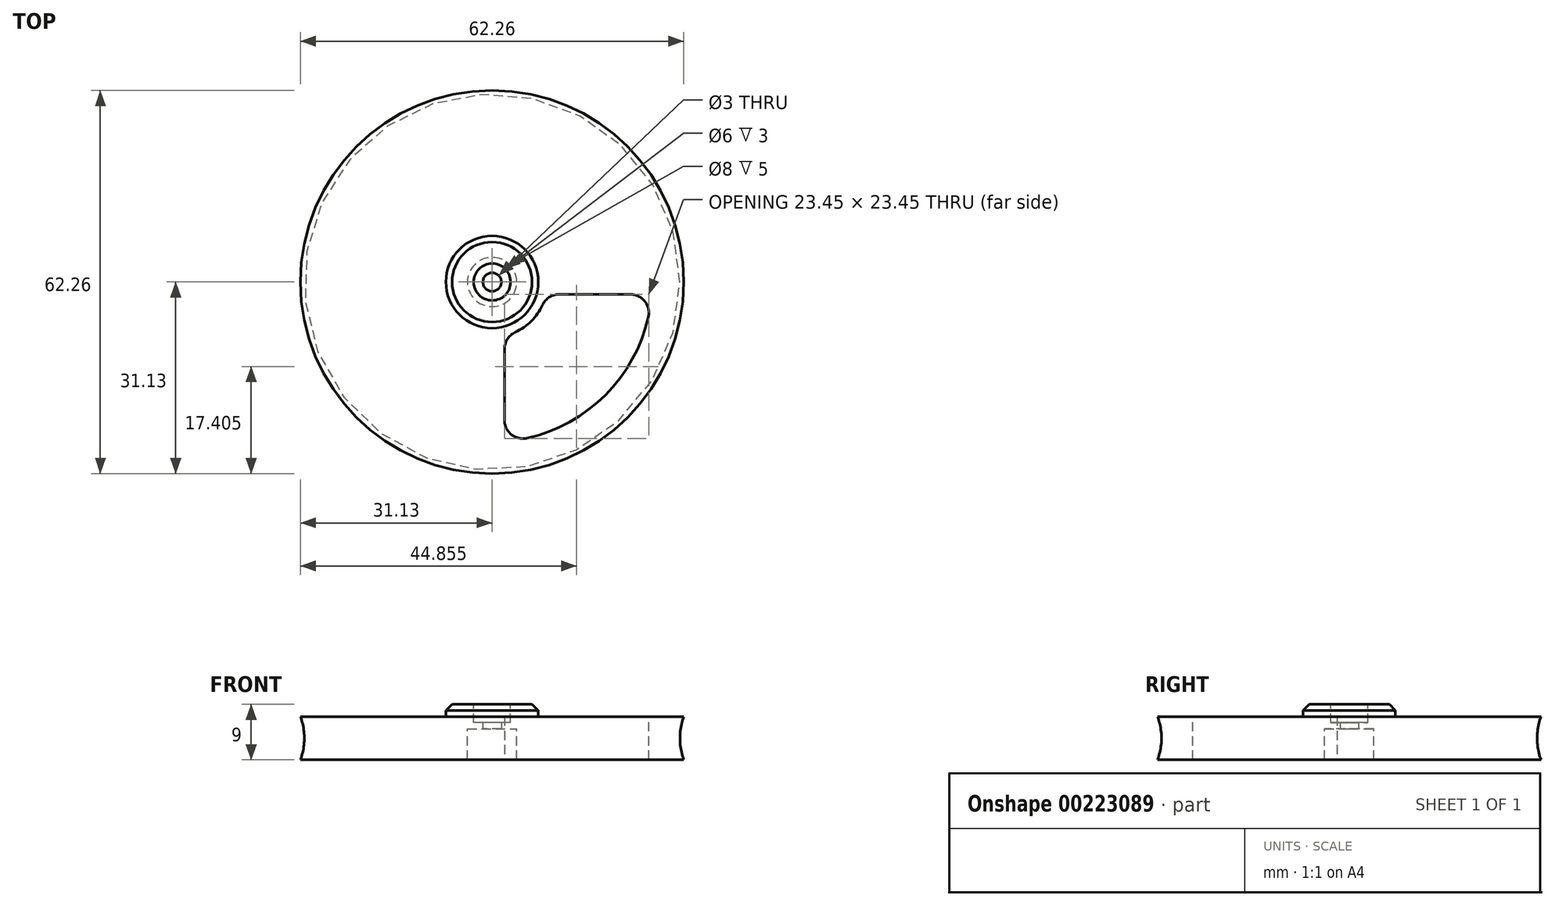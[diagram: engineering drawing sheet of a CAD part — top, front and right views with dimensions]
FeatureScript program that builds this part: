
annotation { "Feature Type Name" : "Feature", "Feature Type Description" : "" }
export const myFeature = defineFeature(function(context is Context, id is Id, definition is map)
    precondition{}
    {
        {
            var Q0;
            Q0=qCreatedBy(makeId("Top.planeOp"),FACE);
            var sketch = newSketch(context, id + "F0", { "sketchPlane" : qUnion([Q0])});
            skCircle(sketch, "E0", {"center": v(0, 0) * mm, "radius": 30 * mm});
            skCircle(sketch, "E1", {"center": v(0, 0) * mm, "radius": 1.5 * mm});
            skSolve(sketch);
        }
        {
            var Q0;
            Q0=makeQuery(id+"F0.imprint","IMPRINT",FACE,{"disambiguationData":[TD([[makeQuery(id+"F0.imprint","IMPRINT",EDGE,{"derivedFrom":sQuery(id+"F0.wireOp",EDGE,"E0")}),1.0]])]});
            extrude(context, id + "F1", {"entities" : qUnion([Q0]), "depth" : 2 * mm});
        }
        {
            var Q0;
            Q0=makeQuery(id+"F1.opExtrude","CAP_FACE",FACE,{"disambiguationData":[OSD([sQuery(id+"F0.wireOp",EDGE,"E0"),sQuery(id+"F0.wireOp",EDGE,"E1")])],"isStart":false});
            var sketch = newSketch(context, id + "F2", { "sketchPlane" : qUnion([Q0])});
            skCircle(sketch, "E2", {"center": v(0, 0) * mm, "radius": 7.5 * mm});
            skSolve(sketch);
        }
        {
            var Q0;
            Q0=makeQuery(id+"F2.imprint","IMPRINT",FACE,{"disambiguationData":[TD([[makeQuery(id+"F2.imprint","IMPRINT",EDGE,{"derivedFrom":sQuery(id+"F2.wireOp",EDGE,"E2")}),1.0]])]});
            extrude(context, id + "F3", {"entities" : qUnion([Q0]), "operationType" : NewBodyOperationType.ADD, "depth" : 2 * mm});
        }
        {
            var Q0;
            Q0=makeQuery(id+"F3.opExtrude","CAP_FACE",FACE,{"disambiguationData":[OSD([sQuery(id+"F0.wireOp",EDGE,"E1"),sQuery(id+"F2.wireOp",EDGE,"E2")])],"isStart":false});
            var sketch = newSketch(context, id + "F4", { "sketchPlane" : qUnion([Q0])});
            skCircle(sketch, "E3", {"center": v(0, 0) * mm, "radius": 3 * mm});
            skSolve(sketch);
        }
        {
            var Q0;
            Q0=makeQuery(id+"F4.imprint","IMPRINT",FACE,{"disambiguationData":[TD([[makeQuery(id+"F4.imprint","IMPRINT",EDGE,{"derivedFrom":sQuery(id+"F4.wireOp",EDGE,"E3")}),1.0]])]});
            extrude(context, id + "F5", {"entities" : qUnion([Q0]), "operationType" : NewBodyOperationType.REMOVE, "oppositeDirection" : true, "depth" : 3 * mm});
        }
        {
            var Q0;
            Q0=makeQuery(id+"F3.opExtrude","CAP_EDGE",EDGE,{"disambiguationData":[OSD([sQuery(id+"F2.wireOp",EDGE,"E2")])],"isStart":false});
            chamfer(context, id + "F6", {"entities" : qUnion([Q0]), "width" : 1 * mm, "tangentPropagation" : true});
        }
        {
            var Q0;
            Q0=makeQuery(id+"F1.opExtrude","CAP_FACE",FACE,{"disambiguationData":[OSD([sQuery(id+"F0.wireOp",EDGE,"E0"),sQuery(id+"F0.wireOp",EDGE,"E1")])],"isStart":true});
            var sketch = newSketch(context, id + "F7", { "sketchPlane" : qUnion([Q0])});
            skCircle(sketch, "E4.0", {"center": v(0, 0) * mm, "radius": 30 * mm});
            skCircle(sketch, "E5", {"center": v(0, 0) * mm, "radius": 4 * mm});
            skSolve(sketch);
        }
        {
            var Q0;
            Q0=makeQuery(id+"F7.imprint","IMPRINT",FACE,{"disambiguationData":[TD([[makeQuery(id+"F7.imprint","IMPRINT",EDGE,{"derivedFrom":sQuery(id+"F7.wireOp",EDGE,"E4.0")}),-1.0]])]});
            extrude(context, id + "F8", {"entities" : qUnion([Q0]), "operationType" : NewBodyOperationType.ADD, "depth" : 5 * mm});
        }
        {
            var Q0;
            Q0=makeQuery(id+"F1.opExtrude","CAP_FACE",FACE,{"disambiguationData":[OSD([sQuery(id+"F0.wireOp",EDGE,"E0"),sQuery(id+"F0.wireOp",EDGE,"E1")])],"isStart":false});
            var sketch = newSketch(context, id + "F9", { "sketchPlane" : qUnion([Q0])});
            skArc(sketch, "E6", {"start": v(2, -25.92) * mm, "mid": v(18.38, -18.38) * mm, "end": v(25.92, -2) * mm});
            skLineSegment(sketch, "E7", {"start": v(25.92, -2) * mm, "end": v(8.77, -2) * mm});
            skArc(sketch, "E8", {"start": v(2, -8.77) * mm, "mid": v(6.36, -6.36) * mm, "end": v(8.77, -2) * mm});
            skLineSegment(sketch, "E9", {"start": v(0, 0) * mm, "end": v(30, 0) * mm, "construction": true});
            skLineSegment(sketch, "E10", {"start": v(0, 0) * mm, "end": v(39.1, -39.1) * mm, "construction": true});
            skLineSegment(sketch, "E11.MirrorCS", {"start": v(2, -25.92) * mm, "end": v(2, -8.77) * mm});
            skSolve(sketch);
        }
        {
            var Q0;
            Q0 = qSketchRegion(id + "F9", true);
            extrude(context, id + "F10", {"entities" : qUnion([Q0]), "operationType" : NewBodyOperationType.REMOVE, "oppositeDirection" : true, "depth" : 25 * mm});
        }
        {
            var Q0;
            Q0=makeQuery(id+"FWcyfWCrI6Tk5ms_1.3.F10.boolean.opBoolean","COPY",EDGE,{"derivedFrom":makeQuery(id+"FWcyfWCrI6Tk5ms_1.3.F10.opExtrude","SWEPT_EDGE",EDGE,{"disambiguationData":[OSD([sQuery(id+"F9.wireOp",EDGE,"E6"),sQuery(id+"F9.wireOp",EDGE,"E7")])]})});
            var Q1;
            Q1=makeQuery(id+"F10.boolean.opBoolean","COPY",EDGE,{"derivedFrom":makeQuery(id+"F10.opExtrude","SWEPT_EDGE",EDGE,{"disambiguationData":[OSD([sQuery(id+"F9.wireOp",EDGE,"E7"),sQuery(id+"F9.wireOp",EDGE,"E8")])]})});
            var Q2;
            Q2=makeQuery(id+"FWcyfWCrI6Tk5ms_1.3.F10.boolean.opBoolean","COPY",EDGE,{"derivedFrom":makeQuery(id+"FWcyfWCrI6Tk5ms_1.3.F10.opExtrude","SWEPT_EDGE",EDGE,{"disambiguationData":[OSD([sQuery(id+"F9.wireOp",EDGE,"E7"),sQuery(id+"F9.wireOp",EDGE,"E8")])]})});
            var Q3;
            Q3=makeQuery(id+"FWcyfWCrI6Tk5ms_1.3.F10.boolean.opBoolean","COPY",EDGE,{"derivedFrom":makeQuery(id+"FWcyfWCrI6Tk5ms_1.3.F10.opExtrude","SWEPT_EDGE",EDGE,{"disambiguationData":[OSD([sQuery(id+"F9.wireOp",EDGE,"E8"),sQuery(id+"F9.wireOp",EDGE,"E11.MirrorCS")])]})});
            var Q4;
            Q4=makeQuery(id+"FWcyfWCrI6Tk5ms_1.2.F10.boolean.opBoolean","COPY",EDGE,{"derivedFrom":makeQuery(id+"FWcyfWCrI6Tk5ms_1.2.F10.opExtrude","SWEPT_EDGE",EDGE,{"disambiguationData":[OSD([sQuery(id+"F9.wireOp",EDGE,"E6"),sQuery(id+"F9.wireOp",EDGE,"E7")])]})});
            var Q5;
            Q5=makeQuery(id+"F10.boolean.opBoolean","COPY",EDGE,{"derivedFrom":makeQuery(id+"F10.opExtrude","SWEPT_EDGE",EDGE,{"disambiguationData":[OSD([sQuery(id+"F9.wireOp",EDGE,"E6"),sQuery(id+"F9.wireOp",EDGE,"E11.MirrorCS")])]})});
            var Q6;
            Q6=makeQuery(id+"FWcyfWCrI6Tk5ms_1.3.F10.boolean.opBoolean","COPY",EDGE,{"derivedFrom":makeQuery(id+"FWcyfWCrI6Tk5ms_1.3.F10.opExtrude","SWEPT_EDGE",EDGE,{"disambiguationData":[OSD([sQuery(id+"F9.wireOp",EDGE,"E6"),sQuery(id+"F9.wireOp",EDGE,"E11.MirrorCS")])]})});
            var Q7;
            Q7=makeQuery(id+"F10.boolean.opBoolean","COPY",EDGE,{"derivedFrom":makeQuery(id+"F10.opExtrude","SWEPT_EDGE",EDGE,{"disambiguationData":[OSD([sQuery(id+"F9.wireOp",EDGE,"E6"),sQuery(id+"F9.wireOp",EDGE,"E7")])]})});
            var Q8;
            Q8=makeQuery(id+"FWcyfWCrI6Tk5ms_1.2.F10.boolean.opBoolean","COPY",EDGE,{"derivedFrom":makeQuery(id+"FWcyfWCrI6Tk5ms_1.2.F10.opExtrude","SWEPT_EDGE",EDGE,{"disambiguationData":[OSD([sQuery(id+"F9.wireOp",EDGE,"E7"),sQuery(id+"F9.wireOp",EDGE,"E8")])]})});
            var Q9;
            Q9=makeQuery(id+"FWcyfWCrI6Tk5ms_1.2.F10.boolean.opBoolean","COPY",EDGE,{"derivedFrom":makeQuery(id+"FWcyfWCrI6Tk5ms_1.2.F10.opExtrude","SWEPT_EDGE",EDGE,{"disambiguationData":[OSD([sQuery(id+"F9.wireOp",EDGE,"E8"),sQuery(id+"F9.wireOp",EDGE,"E11.MirrorCS")])]})});
            var Q10;
            Q10=makeQuery(id+"FWcyfWCrI6Tk5ms_1.2.F10.boolean.opBoolean","COPY",EDGE,{"derivedFrom":makeQuery(id+"FWcyfWCrI6Tk5ms_1.2.F10.opExtrude","SWEPT_EDGE",EDGE,{"disambiguationData":[OSD([sQuery(id+"F9.wireOp",EDGE,"E6"),sQuery(id+"F9.wireOp",EDGE,"E11.MirrorCS")])]})});
            var Q11;
            Q11=makeQuery(id+"FWcyfWCrI6Tk5ms_1.1.F10.boolean.opBoolean","COPY",EDGE,{"derivedFrom":makeQuery(id+"FWcyfWCrI6Tk5ms_1.1.F10.opExtrude","SWEPT_EDGE",EDGE,{"disambiguationData":[OSD([sQuery(id+"F9.wireOp",EDGE,"E7"),sQuery(id+"F9.wireOp",EDGE,"E8")])]})});
            var Q12;
            Q12=makeQuery(id+"FWcyfWCrI6Tk5ms_1.1.F10.boolean.opBoolean","COPY",EDGE,{"derivedFrom":makeQuery(id+"FWcyfWCrI6Tk5ms_1.1.F10.opExtrude","SWEPT_EDGE",EDGE,{"disambiguationData":[OSD([sQuery(id+"F9.wireOp",EDGE,"E8"),sQuery(id+"F9.wireOp",EDGE,"E11.MirrorCS")])]})});
            var Q13;
            Q13=makeQuery(id+"FWcyfWCrI6Tk5ms_1.1.F10.boolean.opBoolean","COPY",EDGE,{"derivedFrom":makeQuery(id+"FWcyfWCrI6Tk5ms_1.1.F10.opExtrude","SWEPT_EDGE",EDGE,{"disambiguationData":[OSD([sQuery(id+"F9.wireOp",EDGE,"E6"),sQuery(id+"F9.wireOp",EDGE,"E11.MirrorCS")])]})});
            var Q14;
            Q14=makeQuery(id+"FWcyfWCrI6Tk5ms_1.1.F10.boolean.opBoolean","COPY",EDGE,{"derivedFrom":makeQuery(id+"FWcyfWCrI6Tk5ms_1.1.F10.opExtrude","SWEPT_EDGE",EDGE,{"disambiguationData":[OSD([sQuery(id+"F9.wireOp",EDGE,"E6"),sQuery(id+"F9.wireOp",EDGE,"E7")])]})});
            var Q15;
            Q15=makeQuery(id+"F10.boolean.opBoolean","COPY",EDGE,{"derivedFrom":makeQuery(id+"F10.opExtrude","SWEPT_EDGE",EDGE,{"disambiguationData":[OSD([sQuery(id+"F9.wireOp",EDGE,"E8"),sQuery(id+"F9.wireOp",EDGE,"E11.MirrorCS")])]})});
            fillet(context, id + "F11", {"entities" : qUnion([Q0, Q1, Q2, Q3, Q4, Q5, Q6, Q7, Q8, Q9, Q10, Q11, Q12, Q13, Q14, Q15]), "radius" : 3 * mm, "tangentPropagation" : true, "allowEdgeOverflow" : false});
        }
        {
            var Q0;
            Q0=qCreatedBy(makeId("Front.planeOp"),FACE);
            var sketch = newSketch(context, id + "F12", { "sketchPlane" : qUnion([Q0])});
            skLineSegment(sketch, "E12", {"start": v(30, 2) * mm, "end": v(30, -5) * mm});
            skLineSegment(sketch, "E13", {"start": v(30, -5) * mm, "end": v(31.13, -5) * mm});
            skLineSegment(sketch, "E14", {"start": v(30, -1.5) * mm, "end": v(37.16, -1.5) * mm, "construction": true});
            skArc(sketch, "E15", {"start": v(31.13, 2) * mm, "mid": v(30.5, -1.5) * mm, "end": v(31.13, -5) * mm});
            skLineSegment(sketch, "E16.MirrorCS", {"start": v(30, 2) * mm, "end": v(31.13, 2) * mm});
            skLineSegment(sketch, "E17", {"start": v(30.5, -1.5) * mm, "end": v(30.5, 5.51) * mm, "construction": true});
            skSolve(sketch);
        }
        {
            var Q0;
            Q0=makeQuery(id+"F12.imprint","IMPRINT",FACE,{"disambiguationData":[TD([[makeQuery(id+"F12.imprint","IMPRINT",EDGE,{"derivedFrom":sQuery(id+"F12.wireOp",EDGE,"E12")}),1.0]])]});
            var Q1;
            Q1=makeQuery(id+"F5.boolean.opBoolean","COPY",FACE,{"derivedFrom":makeQuery(id+"F5.opExtrude","SWEPT_FACE",FACE,{"disambiguationData":[OSD([sQuery(id+"F4.wireOp",EDGE,"E3")])]})});
            revolve(context, id + "F13", {"operationType" : NewBodyOperationType.ADD, "entities" : qUnion([Q0]), "axis" : qUnion([Q1]), "revolveType" : RevolveType.FULL});
        }
    });
